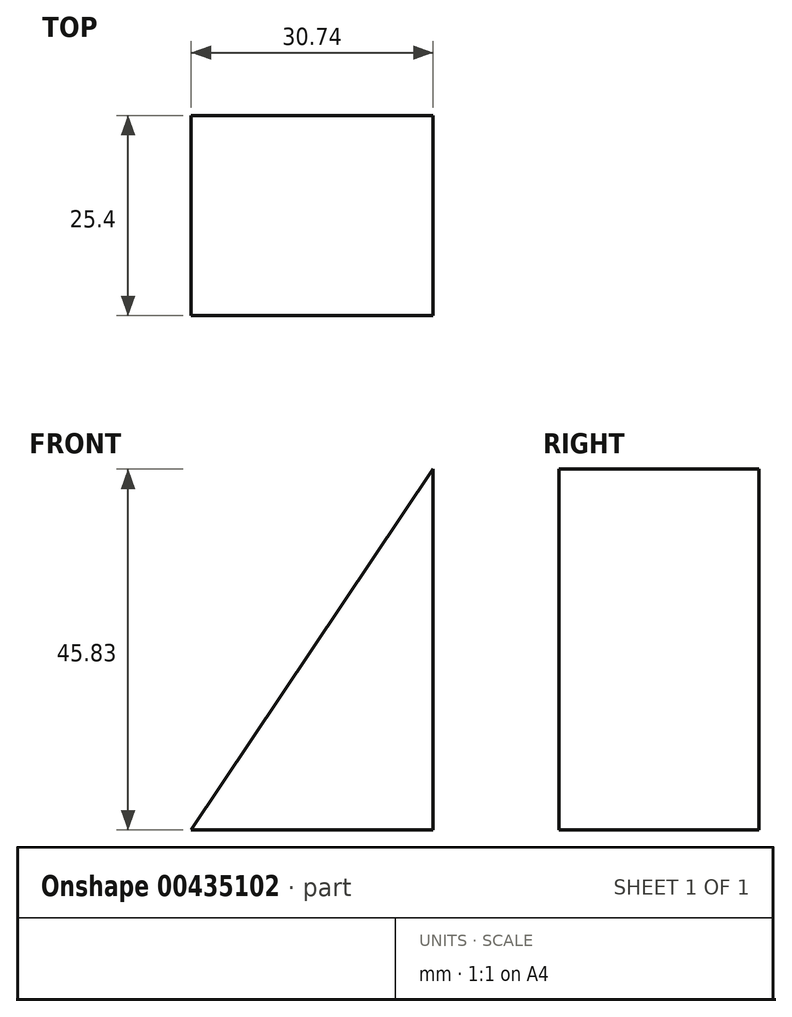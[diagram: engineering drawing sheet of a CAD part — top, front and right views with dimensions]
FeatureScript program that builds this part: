
annotation { "Feature Type Name" : "Feature", "Feature Type Description" : "" }
export const myFeature = defineFeature(function(context is Context, id is Id, definition is map)
    precondition{}
    {
        {
            var Q0;
            Q0=qCreatedBy(makeId("Front.planeOp"),FACE);
            var sketch = newSketch(context, id + "F0", { "sketchPlane" : qUnion([Q0])});
            skLineSegment(sketch, "E0", {"start": v(0, 45.83) * mm, "end": v(0, 0) * mm});
            skLineSegment(sketch, "E1", {"start": v(0, 0) * mm, "end": v(-30.74, 0) * mm});
            skLineSegment(sketch, "E2", {"start": v(-30.74, 0) * mm, "end": v(0, 45.83) * mm});
            skSolve(sketch);
        }
        {
            var Q0;
            Q0=makeQuery(id+"F0.imprint","IMPRINT",FACE,{"disambiguationData":[TD([[makeQuery(id+"F0.imprint","IMPRINT",EDGE,{"derivedFrom":sQuery(id+"F0.wireOp",EDGE,"E0")}),-1.0]])]});
            extrude(context, id + "F1", {"entities" : qUnion([Q0]), "depth" : 25.4 * mm});
        }
    });
